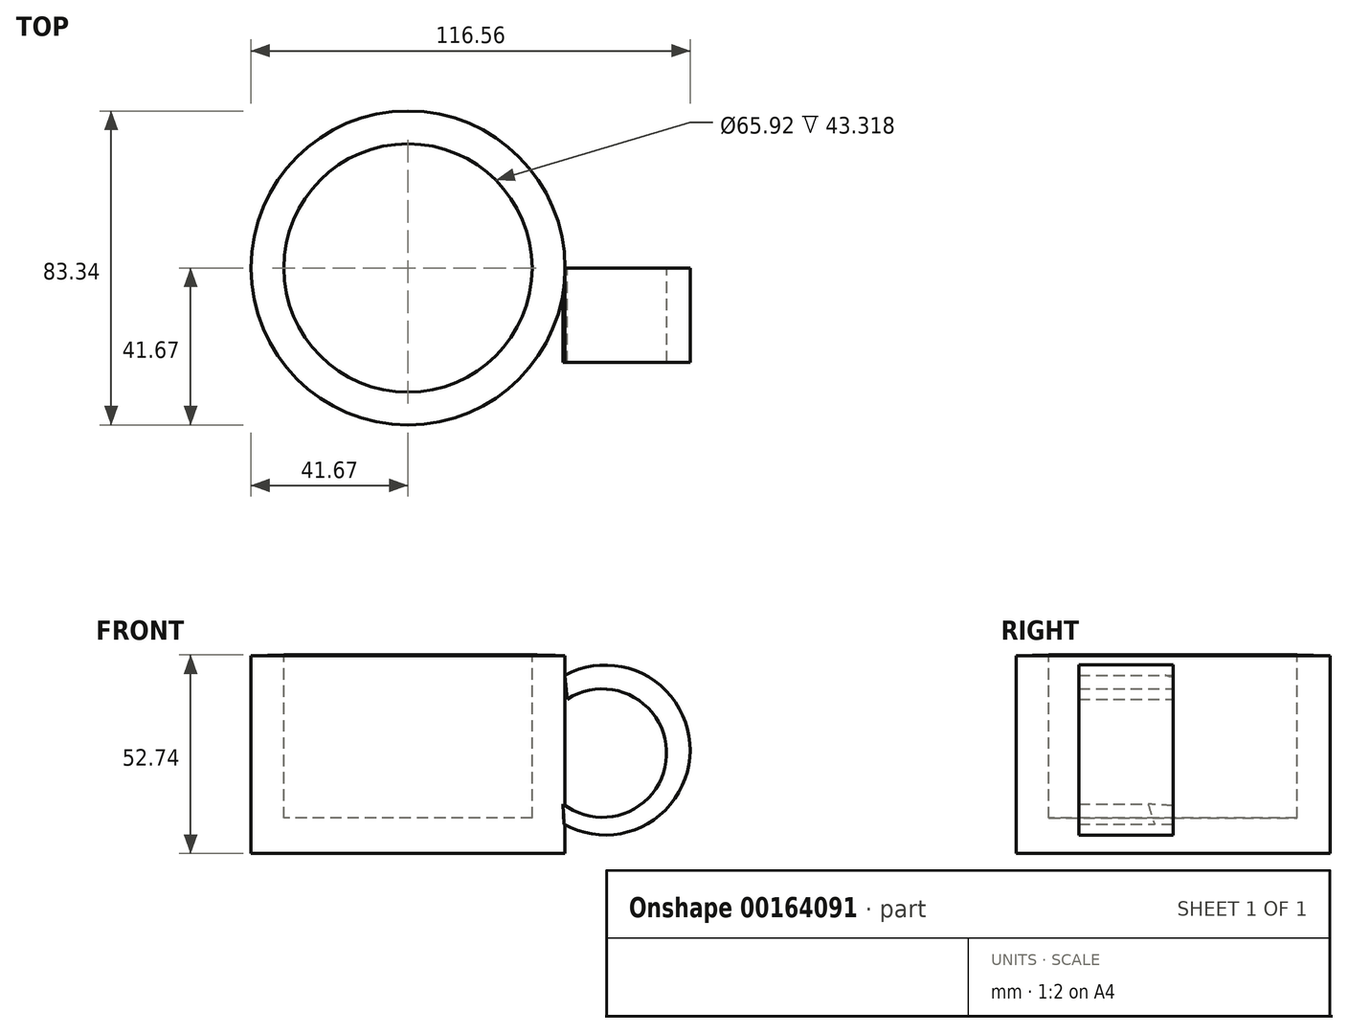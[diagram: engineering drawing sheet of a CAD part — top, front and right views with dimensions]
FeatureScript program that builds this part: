
annotation { "Feature Type Name" : "Feature", "Feature Type Description" : "" }
export const myFeature = defineFeature(function(context is Context, id is Id, definition is map)
    precondition{}
    {
        {
            var Q0;
            Q0=qCreatedBy(makeId("Front.planeOp"),FACE);
            var sketch = newSketch(context, id + "F0", { "sketchPlane" : qUnion([Q0])});
            skLineSegment(sketch, "E0", {"start": v(-16.48, 68.63) * mm, "end": v(-16.48, 25.3) * mm});
            skLineSegment(sketch, "E1", {"start": v(-16.48, 25.3) * mm, "end": v(-49.44, 25.3) * mm});
            skLineSegment(sketch, "E2", {"start": v(-7.77, 19.66) * mm, "end": v(-7.77, 68.4) * mm});
            skLineSegment(sketch, "E3", {"start": v(-16.48, 68.63) * mm, "end": v(-7.77, 68.4) * mm});
            skLineSegment(sketch, "E4", {"start": v(-49.44, 25.3) * mm, "end": v(-49.44, 15.9) * mm});
            skLineSegment(sketch, "E5", {"start": v(-49.44, 15.9) * mm, "end": v(-7.77, 15.9) * mm});
            skLineSegment(sketch, "E6", {"start": v(-7.77, 19.66) * mm, "end": v(-7.77, 15.9) * mm});
            skSolve(sketch);
        }
        {
            var Q0;
            Q0=makeQuery(id+"F0.imprint","IMPRINT",FACE,{"disambiguationData":[TD([[makeQuery(id+"F0.imprint","IMPRINT",EDGE,{"derivedFrom":sQuery(id+"F0.wireOp",EDGE,"E0")}),1.0]])]});
            var Q1;
            Q1=sQuery(id+"F0.wireOp",EDGE,"E4");
            revolve(context, id + "F1", {"entities" : qUnion([Q0]), "axis" : qUnion([Q1]), "revolveType" : RevolveType.FULL});
        }
        {
            var Q0;
            Q0=qCreatedBy(makeId("Front.planeOp"),FACE);
            var sketch = newSketch(context, id + "F2", { "sketchPlane" : qUnion([Q0])});
            skArc(sketch, "E7", {"start": v(-8.3, 29.08) * mm, "mid": v(19.18, 41.83) * mm, "end": v(-7.11, 56.86) * mm});
            skArc(sketch, "E8", {"start": v(-8.05, 23.66) * mm, "mid": v(25.45, 43.24) * mm, "end": v(-7.82, 63.21) * mm});
            skLineSegment(sketch, "E9", {"start": v(-8.3, 29.08) * mm, "end": v(-8.05, 23.66) * mm});
            skLineSegment(sketch, "E10", {"start": v(-7.11, 56.86) * mm, "end": v(-7.82, 63.21) * mm});
            skSolve(sketch);
        }
        {
            var Q0;
            Q0 = qSketchRegion(id + "F2", true);
            extrude(context, id + "F3", {"entities" : qUnion([Q0]), "operationType" : NewBodyOperationType.ADD, "depth" : 25 * mm});
        }
    });
